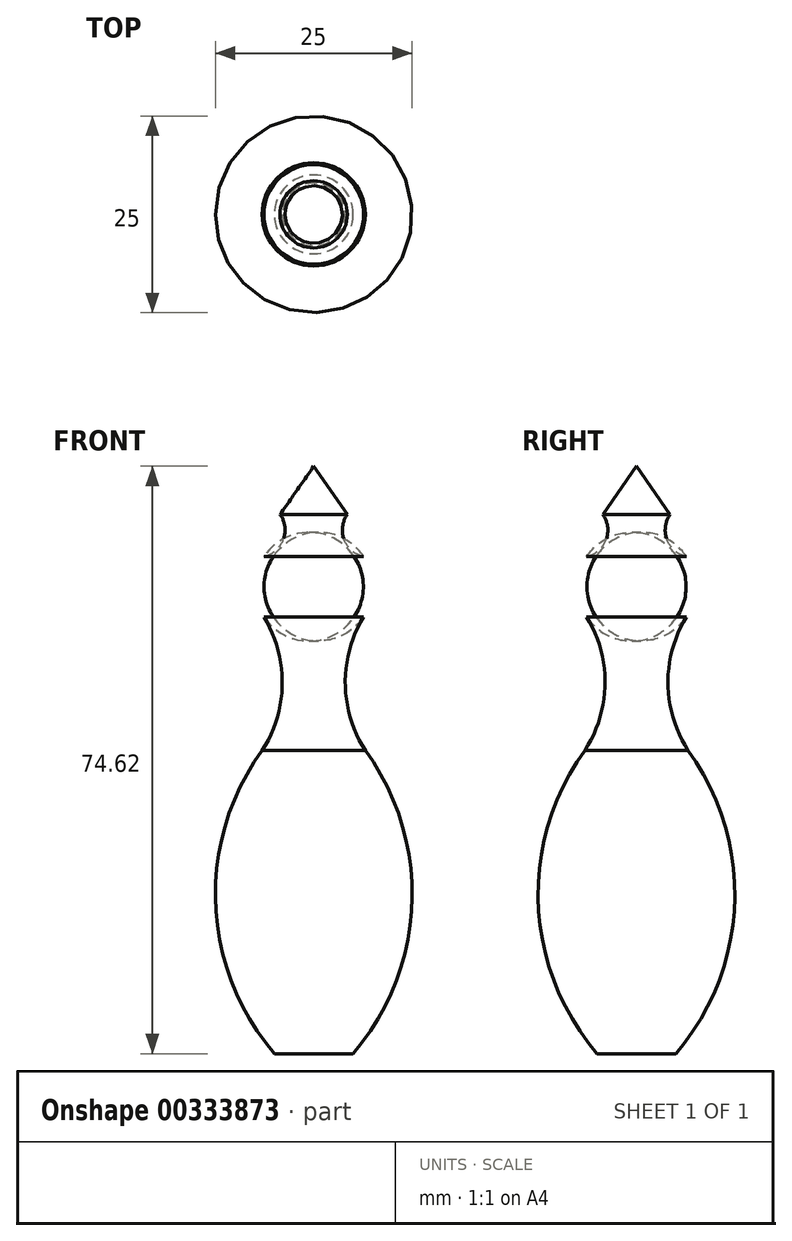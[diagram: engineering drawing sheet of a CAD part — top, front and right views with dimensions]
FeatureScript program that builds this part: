
annotation { "Feature Type Name" : "Feature", "Feature Type Description" : "" }
export const myFeature = defineFeature(function(context is Context, id is Id, definition is map)
    precondition{}
    {
        {
            var Q0;
            Q0=qCreatedBy(makeId("Front.planeOp"),FACE);
            var sketch = newSketch(context, id + "F0", { "sketchPlane" : qUnion([Q0])});
            skLineSegment(sketch, "E0", {"start": v(0, 0) * mm, "end": v(4.27, -6.12) * mm});
            skArc(sketch, "E1", {"start": v(6.34, -19.12) * mm, "mid": v(7.5, -15.3) * mm, "end": v(6.34, -11.47) * mm});
            skArc(sketch, "E2", {"start": v(4.27, -6.12) * mm, "mid": v(3.88, -9.34) * mm, "end": v(6.34, -11.47) * mm});
            skArc(sketch, "E3", {"start": v(6.34, -19.12) * mm, "mid": v(4, -27.64) * mm, "end": v(6.55, -36.1) * mm});
            skArc(sketch, "E4", {"start": v(5, -74.62) * mm, "mid": v(12.47, -55.62) * mm, "end": v(6.55, -36.1) * mm});
            skLineSegment(sketch, "E5", {"start": v(5, -74.62) * mm, "end": v(0, -74.62) * mm});
            skLineSegment(sketch, "E6", {"start": v(0, -74.62) * mm, "end": v(0, 0) * mm});
            skSolve(sketch);
        }
        {
            var Q0;
            Q0 = qSketchRegion(id + "F0", true);
            var Q1;
            Q1=sQuery(id+"F0.wireOp",EDGE,"E6");
            revolve(context, id + "F1", {"entities" : qUnion([Q0]), "axis" : qUnion([Q1]), "revolveType" : RevolveType.FULL});
        }
    });
